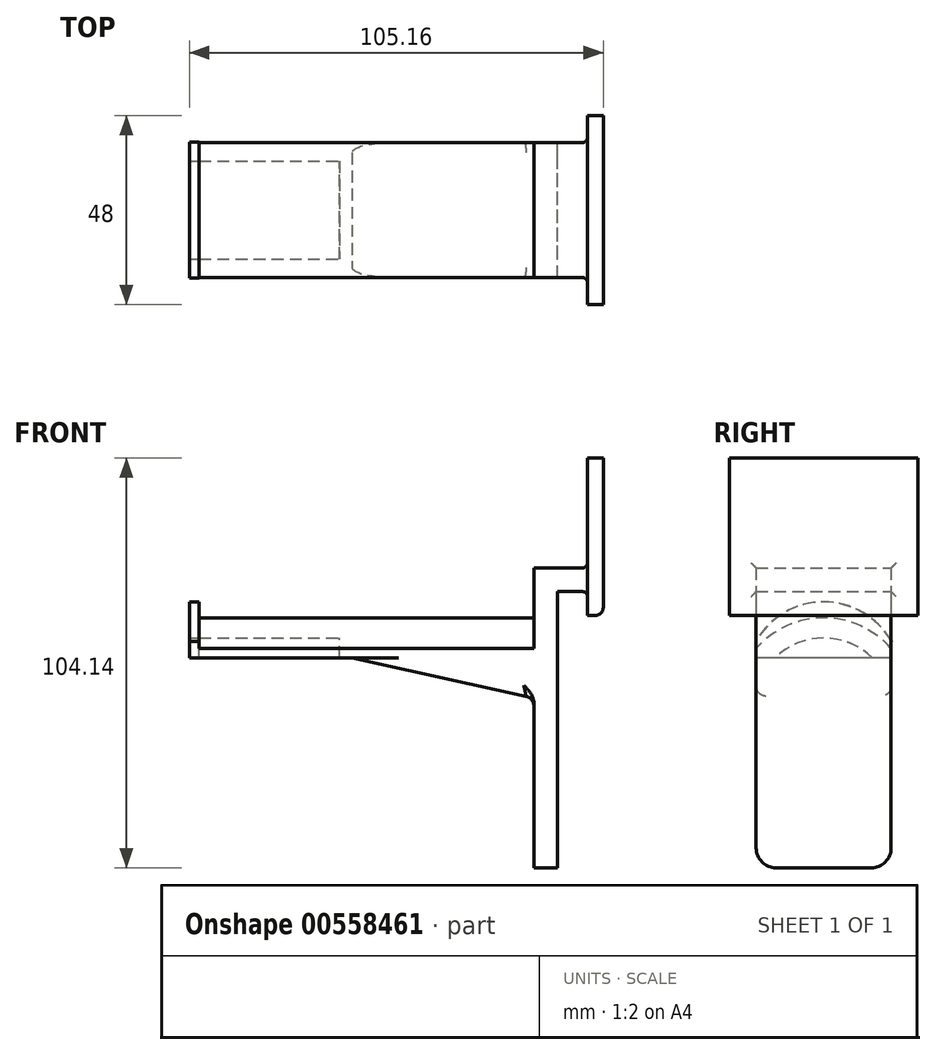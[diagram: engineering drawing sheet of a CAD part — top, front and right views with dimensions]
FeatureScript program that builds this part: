
annotation { "Feature Type Name" : "Feature", "Feature Type Description" : "" }
export const myFeature = defineFeature(function(context is Context, id is Id, definition is map)
    precondition{}
    {
        {
            var Q0;
            Q0=qCreatedBy(makeId("Front.planeOp"),FACE);
            var sketch = newSketch(context, id + "F0", { "sketchPlane" : qUnion([Q0])});
            skLineSegment(sketch, "E0.bottom", {"start": v(0, 0) * mm, "end": v(4, 0) * mm});
            skLineSegment(sketch, "E0.top", {"start": v(0, 40) * mm, "end": v(4, 40) * mm});
            skLineSegment(sketch, "E0.left", {"start": v(0, 0) * mm, "end": v(0, 40) * mm});
            skLineSegment(sketch, "E0.right", {"start": v(4, 0) * mm, "end": v(4, 40) * mm});
            skLineSegment(sketch, "E1.bottom", {"start": v(0, 12.06) * mm, "end": v(-7.62, 12.06) * mm});
            skLineSegment(sketch, "E1.top", {"start": v(0, 6.06) * mm, "end": v(-7.62, 6.06) * mm});
            skLineSegment(sketch, "E1.left", {"start": v(0, 12.06) * mm, "end": v(0, 6.06) * mm});
            skLineSegment(sketch, "E1.right", {"start": v(-7.62, 12.06) * mm, "end": v(-7.62, 6.06) * mm});
            skLineSegment(sketch, "E2.bottom", {"start": v(-7.62, 12.06) * mm, "end": v(-13.62, 12.06) * mm});
            skLineSegment(sketch, "E2.top", {"start": v(-7.62, -64.14) * mm, "end": v(-13.62, -64.14) * mm});
            skLineSegment(sketch, "E2.left", {"start": v(-7.62, 12.06) * mm, "end": v(-7.62, -64.14) * mm});
            skLineSegment(sketch, "E2.right", {"start": v(-13.62, 12.06) * mm, "end": v(-13.62, -64.14) * mm});
            skSolve(sketch);
        }
        {
            var Q0;
            {var subQ3=sQuery(id+"F0.wireOp",EDGE,"E0.bottom");Q0=makeQuery(id+"F0.imprint","IMPRINT",FACE,{"disambiguationData":[TD([[makeQuery(id+"F0.imprint","IMPRINT",EDGE,{"derivedFrom":subQ3}),1.0]])]});}
            var Q1;
            {var subQ0=sQuery(id+"F0.wireOp",EDGE,"E1.bottom");Q1=makeQuery(id+"F0.imprint","IMPRINT",FACE,{"disambiguationData":[TD([[makeQuery(id+"F0.imprint","IMPRINT",EDGE,{"derivedFrom":subQ0}),1.0]])]});}
            extrude(context, id + "F1", {"entities" : qUnion([Q0, Q1]), "endBound" : BoundingType.SYMMETRIC, "depth" : 34.3 * mm});
        }
        {
            var Q0;
            {var subQ3=sQuery(id+"F0.wireOp",EDGE,"E2.bottom");Q0=makeQuery(id+"F0.imprint","IMPRINT",FACE,{"disambiguationData":[TD([[makeQuery(id+"F0.imprint","IMPRINT",EDGE,{"derivedFrom":subQ3}),1.0]])]});}
            extrude(context, id + "F2", {"entities" : qUnion([Q0]), "operationType" : NewBodyOperationType.ADD, "endBound" : BoundingType.SYMMETRIC, "depth" : 34.3 * mm});
        }
        {
            var Q0;
            {var subQ3=sQuery(id+"F0.wireOp",EDGE,"E0.bottom");Q0=makeQuery(id+"F0.imprint","IMPRINT",FACE,{"disambiguationData":[TD([[makeQuery(id+"F0.imprint","IMPRINT",EDGE,{"derivedFrom":subQ3}),1.0]])]});}
            extrude(context, id + "F3", {"entities" : qUnion([Q0]), "operationType" : NewBodyOperationType.ADD, "endBound" : BoundingType.SYMMETRIC, "depth" : 48 * mm, "offsetDistance" : 25 * mm});
        }
        {
            var Q0;
            Q0=makeQuery(id+"F1.opExtrude","SWEPT_EDGE",EDGE,{"disambiguationData":[OSD([sQuery(id+"F0.wireOp",EDGE,"E0.left"),sQuery(id+"F0.wireOp",EDGE,"E1.bottom"),sQuery(id+"F0.wireOp",EDGE,"E1.left")])]});
            var Q1;
            Q1=makeQuery(id+"F1.opExtrude","SWEPT_EDGE",EDGE,{"disambiguationData":[OSD([sQuery(id+"F0.wireOp",EDGE,"E0.left"),sQuery(id+"F0.wireOp",EDGE,"E1.top"),sQuery(id+"F0.wireOp",EDGE,"E1.left")])]});
            var Q2;
            Q2=makeQuery(id+"F1.opExtrude","SWEPT_EDGE",EDGE,{"disambiguationData":[OSD([sQuery(id+"F0.wireOp",EDGE,"E1.top"),sQuery(id+"F0.wireOp",EDGE,"E2.left")])]});
            var Q3;
            {var subQ0=sQuery(id+"F0.wireOp",EDGE,"E0.left");var subQ1=sQuery(id+"F0.wireOp",EDGE,"E2.left");Q3=makeQuery(id+"F3.boolean.opBoolean","INTERSECT",EDGE,{"derivedFrom":[makeQuery(id+"F2.boolean.opBoolean","MERGE",FACE,{"derivedFrom":[makeQuery(id+"F1.opExtrude","CAP_FACE",FACE,{"disambiguationData":[OSD([sQuery(id+"F0.wireOp",EDGE,"E0.bottom"),sQuery(id+"F0.wireOp",EDGE,"E0.top"),subQ0,sQuery(id+"F0.wireOp",EDGE,"E0.right"),sQuery(id+"F0.wireOp",EDGE,"E1.bottom"),sQuery(id+"F0.wireOp",EDGE,"E1.top"),subQ1])],"isStart":false}),makeQuery(id+"F2.opExtrude","CAP_FACE",FACE,{"disambiguationData":[OSD([sQuery(id+"F0.wireOp",EDGE,"E2.bottom"),sQuery(id+"F0.wireOp",EDGE,"E2.top"),subQ1,sQuery(id+"F0.wireOp",EDGE,"E2.right")])],"isStart":false})]}),makeQuery(id+"F3.opExtrude","SWEPT_FACE",FACE,{"disambiguationData":[OSD([subQ0,sQuery(id+"F0.wireOp",EDGE,"E1.left")])]})]});}
            var Q4;
            {var subQ0=sQuery(id+"F0.wireOp",EDGE,"E0.left");var subQ1=sQuery(id+"F0.wireOp",EDGE,"E2.left");Q4=makeQuery(id+"F3.boolean.opBoolean","INTERSECT",EDGE,{"derivedFrom":[makeQuery(id+"F2.boolean.opBoolean","MERGE",FACE,{"derivedFrom":[makeQuery(id+"F1.opExtrude","CAP_FACE",FACE,{"disambiguationData":[OSD([sQuery(id+"F0.wireOp",EDGE,"E0.bottom"),sQuery(id+"F0.wireOp",EDGE,"E0.top"),subQ0,sQuery(id+"F0.wireOp",EDGE,"E0.right"),sQuery(id+"F0.wireOp",EDGE,"E1.bottom"),sQuery(id+"F0.wireOp",EDGE,"E1.top"),subQ1])],"isStart":true}),makeQuery(id+"F2.opExtrude","CAP_FACE",FACE,{"disambiguationData":[OSD([sQuery(id+"F0.wireOp",EDGE,"E2.bottom"),sQuery(id+"F0.wireOp",EDGE,"E2.top"),subQ1,sQuery(id+"F0.wireOp",EDGE,"E2.right")])],"isStart":true})]}),makeQuery(id+"F3.opExtrude","SWEPT_FACE",FACE,{"disambiguationData":[OSD([subQ0,sQuery(id+"F0.wireOp",EDGE,"E1.left")])]})]});}
            fillet(context, id + "F4", {"entities" : qUnion([Q0, Q1, Q2, Q3, Q4]), "radius" : 1.27 * mm, "tangentPropagation" : true, "allowEdgeOverflow" : false});
        }
        {
            var Q0;
            Q0=makeQuery(id+"F2.opExtrude","SWEPT_FACE",FACE,{"disambiguationData":[OSD([sQuery(id+"F0.wireOp",EDGE,"E2.right")])]});
            var sketch = newSketch(context, id + "F5", { "sketchPlane" : qUnion([Q0])});
            skArc(sketch, "E3", {"start": v(19, -10.8) * mm, "mid": v(0, -0.64) * mm, "end": v(-19, -10.8) * mm});
            skArc(sketch, "E4.0", {"start": v(12.44, -10.8) * mm, "mid": v(0, -5.72) * mm, "end": v(-12.44, -10.8) * mm});
            skLineSegment(sketch, "E5", {"start": v(-19, -10.8) * mm, "end": v(-12.44, -10.8) * mm});
            skLineSegment(sketch, "E6", {"start": v(12.44, -10.8) * mm, "end": v(19, -10.8) * mm});
            skSolve(sketch);
        }
        {
            var Q0;
            Q0=qSketchRegion(id+"F5",true);
            extrude(context, id + "F6", {"entities" : qUnion([Q0]), "operationType" : NewBodyOperationType.ADD, "depth" : 85 * mm, "offsetDistance" : 25 * mm});
        }
        {
            var Q0;
            Q0=makeQuery(id+"F6.opExtrude","CAP_FACE",FACE,{"disambiguationData":[OSD([sQuery(id+"F5.wireOp",EDGE,"E3"),sQuery(id+"F5.wireOp",EDGE,"E4.0"),sQuery(id+"F5.wireOp",EDGE,"E5"),sQuery(id+"F5.wireOp",EDGE,"E6")])],"isStart":false});
            var sketch = newSketch(context, id + "F7", { "sketchPlane" : qUnion([Q0])});
            skArc(sketch, "E7", {"start": v(19, -10.8) * mm, "mid": v(0, 3.42) * mm, "end": v(-19, -10.8) * mm});
            skArc(sketch, "E8", {"start": v(12.44, -10.8) * mm, "mid": v(0, -5.73) * mm, "end": v(-12.44, -10.8) * mm});
            skLineSegment(sketch, "E9", {"start": v(-12.44, -10.8) * mm, "end": v(-19, -10.8) * mm});
            skLineSegment(sketch, "E10", {"start": v(12.44, -10.8) * mm, "end": v(19, -10.8) * mm});
            skSolve(sketch);
        }
        {
            var Q0;
            Q0=qSketchRegion(id+"F7",true);
            extrude(context, id + "F8", {"entities" : qUnion([Q0]), "operationType" : NewBodyOperationType.ADD, "depth" : 2.54 * mm});
        }
        {
            var Q0;
            Q0=makeQuery(id+"F2.opExtrude","CAP_EDGE",EDGE,{"disambiguationData":[OSD([sQuery(id+"F0.wireOp",EDGE,"E2.top")])],"isStart":false});
            var Q1;
            Q1=makeQuery(id+"F2.opExtrude","CAP_EDGE",EDGE,{"disambiguationData":[OSD([sQuery(id+"F0.wireOp",EDGE,"E2.top")])],"isStart":true});
            fillet(context, id + "F9", {"entities" : qUnion([Q0, Q1]), "radius" : 5.08 * mm, "tangentPropagation" : true, "allowEdgeOverflow" : false});
        }
        {
            var Q0;
            Q0=makeQuery(id+"F8.opExtrude","CAP_FACE",FACE,{"disambiguationData":[OSD([sQuery(id+"F7.wireOp",EDGE,"E7"),sQuery(id+"F7.wireOp",EDGE,"E8"),sQuery(id+"F7.wireOp",EDGE,"E9"),sQuery(id+"F7.wireOp",EDGE,"E10")])],"isStart":false});
            var sketch = newSketch(context, id + "F10", { "sketchPlane" : qUnion([Q0])});
            skLineSegment(sketch, "E11.bottom", {"start": v(-22.66, -6.6) * mm, "end": v(-17.15, -6.6) * mm});
            skLineSegment(sketch, "E11.top", {"start": v(-22.66, -15.65) * mm, "end": v(-17.15, -15.65) * mm});
            skLineSegment(sketch, "E11.left", {"start": v(-22.66, -6.6) * mm, "end": v(-22.66, -15.65) * mm});
            skLineSegment(sketch, "E11.right", {"start": v(-17.15, -6.6) * mm, "end": v(-17.15, -15.65) * mm});
            skLineSegment(sketch, "E12.MirrorCS", {"start": v(17.15, -6.6) * mm, "end": v(17.15, -15.65) * mm});
            skLineSegment(sketch, "E13.MirrorCS", {"start": v(22.66, -15.65) * mm, "end": v(17.15, -15.65) * mm});
            skLineSegment(sketch, "E14.MirrorCS", {"start": v(22.66, -6.6) * mm, "end": v(17.15, -6.6) * mm});
            skLineSegment(sketch, "E15.MirrorCS", {"start": v(22.66, -6.6) * mm, "end": v(22.66, -15.65) * mm});
            skSolve(sketch);
        }
        {
            var Q0;
            Q0=qSketchRegion(id+"F10",true);
            extrude(context, id + "F11", {"entities" : qUnion([Q0]), "operationType" : NewBodyOperationType.REMOVE, "oppositeDirection" : true, "depth" : 88.9 * mm});
        }
        {
            var Q0;
            {var subQ0=sQuery(id+"F0.wireOp",EDGE,"E2.left");Q0=makeQuery(id+"F11.boolean.opBoolean","MERGE",FACE,{"derivedFrom":[makeQuery(id+"F2.boolean.opBoolean","MERGE",FACE,{"derivedFrom":[makeQuery(id+"F1.opExtrude","CAP_FACE",FACE,{"disambiguationData":[OSD([sQuery(id+"F0.wireOp",EDGE,"E0.bottom"),sQuery(id+"F0.wireOp",EDGE,"E0.top"),sQuery(id+"F0.wireOp",EDGE,"E0.left"),sQuery(id+"F0.wireOp",EDGE,"E0.right"),sQuery(id+"F0.wireOp",EDGE,"E1.bottom"),sQuery(id+"F0.wireOp",EDGE,"E1.top"),subQ0])],"isStart":false}),makeQuery(id+"F2.opExtrude","CAP_FACE",FACE,{"disambiguationData":[OSD([sQuery(id+"F0.wireOp",EDGE,"E2.bottom"),sQuery(id+"F0.wireOp",EDGE,"E2.top"),subQ0,sQuery(id+"F0.wireOp",EDGE,"E2.right")])],"isStart":false})]}),makeQuery(id+"F11.opExtrude","SWEPT_FACE",FACE,{"disambiguationData":[OSD([sQuery(id+"F10.wireOp",EDGE,"E12.MirrorCS")])]})]});}
            var sketch = newSketch(context, id + "F12", { "sketchPlane" : qUnion([Q0])});
            skLineSegment(sketch, "E16", {"start": v(-13.62, -20.96) * mm, "end": v(-59.8, -10.8) * mm});
            skLineSegment(sketch, "E17", {"start": v(-59.8, -10.8) * mm, "end": v(-13.62, -10.8) * mm});
            skLineSegment(sketch, "E18", {"start": v(-13.62, -10.8) * mm, "end": v(-13.62, -20.96) * mm});
            skSolve(sketch);
        }
        {
            var Q0;
            Q0=makeQuery(id+"F12.imprint","IMPRINT",FACE,{"disambiguationData":[TD([[makeQuery(id+"F12.imprint","IMPRINT",EDGE,{"derivedFrom":sQuery(id+"F12.wireOp",EDGE,"E16")}),-1.0]])]});
            var Q1;
            {var subQ0=sQuery(id+"F0.wireOp",EDGE,"E2.left");Q1=makeQuery(id+"F11.boolean.opBoolean","MERGE",FACE,{"derivedFrom":[makeQuery(id+"F2.boolean.opBoolean","MERGE",FACE,{"derivedFrom":[makeQuery(id+"F1.opExtrude","CAP_FACE",FACE,{"disambiguationData":[OSD([sQuery(id+"F0.wireOp",EDGE,"E0.bottom"),sQuery(id+"F0.wireOp",EDGE,"E0.top"),sQuery(id+"F0.wireOp",EDGE,"E0.left"),sQuery(id+"F0.wireOp",EDGE,"E0.right"),sQuery(id+"F0.wireOp",EDGE,"E1.bottom"),sQuery(id+"F0.wireOp",EDGE,"E1.top"),subQ0])],"isStart":true}),makeQuery(id+"F2.opExtrude","CAP_FACE",FACE,{"disambiguationData":[OSD([sQuery(id+"F0.wireOp",EDGE,"E2.bottom"),sQuery(id+"F0.wireOp",EDGE,"E2.top"),subQ0,sQuery(id+"F0.wireOp",EDGE,"E2.right")])],"isStart":true})]}),makeQuery(id+"F11.opExtrude","SWEPT_FACE",FACE,{"disambiguationData":[OSD([sQuery(id+"F10.wireOp",EDGE,"E11.right")])]})]});}
            extrude(context, id + "F13", {"entities" : qUnion([Q0]), "operationType" : NewBodyOperationType.ADD, "endBound" : BoundingType.UP_TO_SURFACE, "oppositeDirection" : true, "endBoundEntityFace" : qUnion([Q1]), "depth" : 25.4 * mm});
        }
        {
            var Q0;
            {var subQ0=sQuery(id+"F5.wireOp",EDGE,"E4.0");var subQ1=makeQuery(id+"F6.opExtrude","SWEPT_FACE",FACE,{"disambiguationData":[OSD([subQ0])]});var subQ2=sQuery(id+"F0.wireOp",EDGE,"E2.right");var subQ4=sQuery(id+"F0.wireOp",EDGE,"E2.top");Q0=makeQuery(id+"F13.boolean.opBoolean","SPLIT",FACE,{"disambiguationData":[TD([subQ1])],"derivedFrom":makeQuery(id+"F6.boolean.opBoolean","SPLIT",FACE,{"disambiguationData":[TD([makeQuery(id+"F2.opExtrude","SWEPT_FACE",FACE,{"disambiguationData":[OSD([subQ4])]})])],"derivedFrom":makeQuery(id+"F2.opExtrude","SWEPT_FACE",FACE,{"disambiguationData":[OSD([subQ2])]})})});}
            extrude(context, id + "F14", {"entities" : qUnion([Q0]), "operationType" : NewBodyOperationType.ADD, "depth" : 49.38 * mm});
        }
        {
            var Q0;
            Q0=makeQuery(id+"F13.opExtrude","CAP_EDGE",EDGE,{"disambiguationData":[OSD([sQuery(id+"F12.wireOp",EDGE,"E16")])],"isStart":false});
            var Q1;
            Q1=makeQuery(id+"F13.opExtrude","CAP_EDGE",EDGE,{"disambiguationData":[OSD([sQuery(id+"F12.wireOp",EDGE,"E16")])],"isStart":true});
            fillet(context, id + "F15", {"entities" : qUnion([Q0, Q1]), "radius" : 2.54 * mm, "tangentPropagation" : true, "allowEdgeOverflow" : false});
        }
        {
            var Q0;
            Q0=makeQuery(id+"F13.opExtrude","SWEPT_EDGE",EDGE,{"disambiguationData":[OSD([sQuery(id+"F0.wireOp",EDGE,"E2.right"),sQuery(id+"F12.wireOp",EDGE,"E16"),sQuery(id+"F12.wireOp",EDGE,"E18")])]});
            fillet(context, id + "F16", {"entities" : qUnion([Q0]), "radius" : 2.54 * mm, "tangentPropagation" : true, "allowEdgeOverflow" : false});
        }
        {
            var Q0;
            Q0=makeQuery(id+"F1.opExtrude","SWEPT_EDGE",EDGE,{"disambiguationData":[OSD([sQuery(id+"F0.wireOp",EDGE,"E0.bottom"),sQuery(id+"F0.wireOp",EDGE,"E0.right")])]});
            fillet(context, id + "F17", {"entities" : qUnion([Q0]), "radius" : 2 * mm, "tangentPropagation" : true, "allowEdgeOverflow" : false});
        }
        {
            var Q0;
            Q0=qCreatedBy(makeId("Front.planeOp"),FACE);
            var sketch = newSketch(context, id + "F18", { "sketchPlane" : qUnion([Q0])});
            skLineSegment(sketch, "E19.bottom", {"start": v(30.65, 62.08) * mm, "end": v(-130.37, 62.08) * mm});
            skLineSegment(sketch, "E19.top", {"start": v(30.65, -78.95) * mm, "end": v(-130.37, -78.95) * mm});
            skLineSegment(sketch, "E19.left", {"start": v(30.65, 62.08) * mm, "end": v(30.65, -78.95) * mm});
            skLineSegment(sketch, "E19.right", {"start": v(-130.37, 62.08) * mm, "end": v(-130.37, -78.95) * mm});
            skSolve(sketch);
        }
        {
            var Q0;
            Q0=qCreatedBy(makeId("Right.planeOp"),FACE);
            cPlane(context, id + "F19", {"entities" : qUnion([Q0]), "cplaneType" : CPlaneType.OFFSET, "offset" : 25 * mm, "oppositeDirection" : true, "width" : 150 * mm, "height" : 150 * mm});
        }
    });
